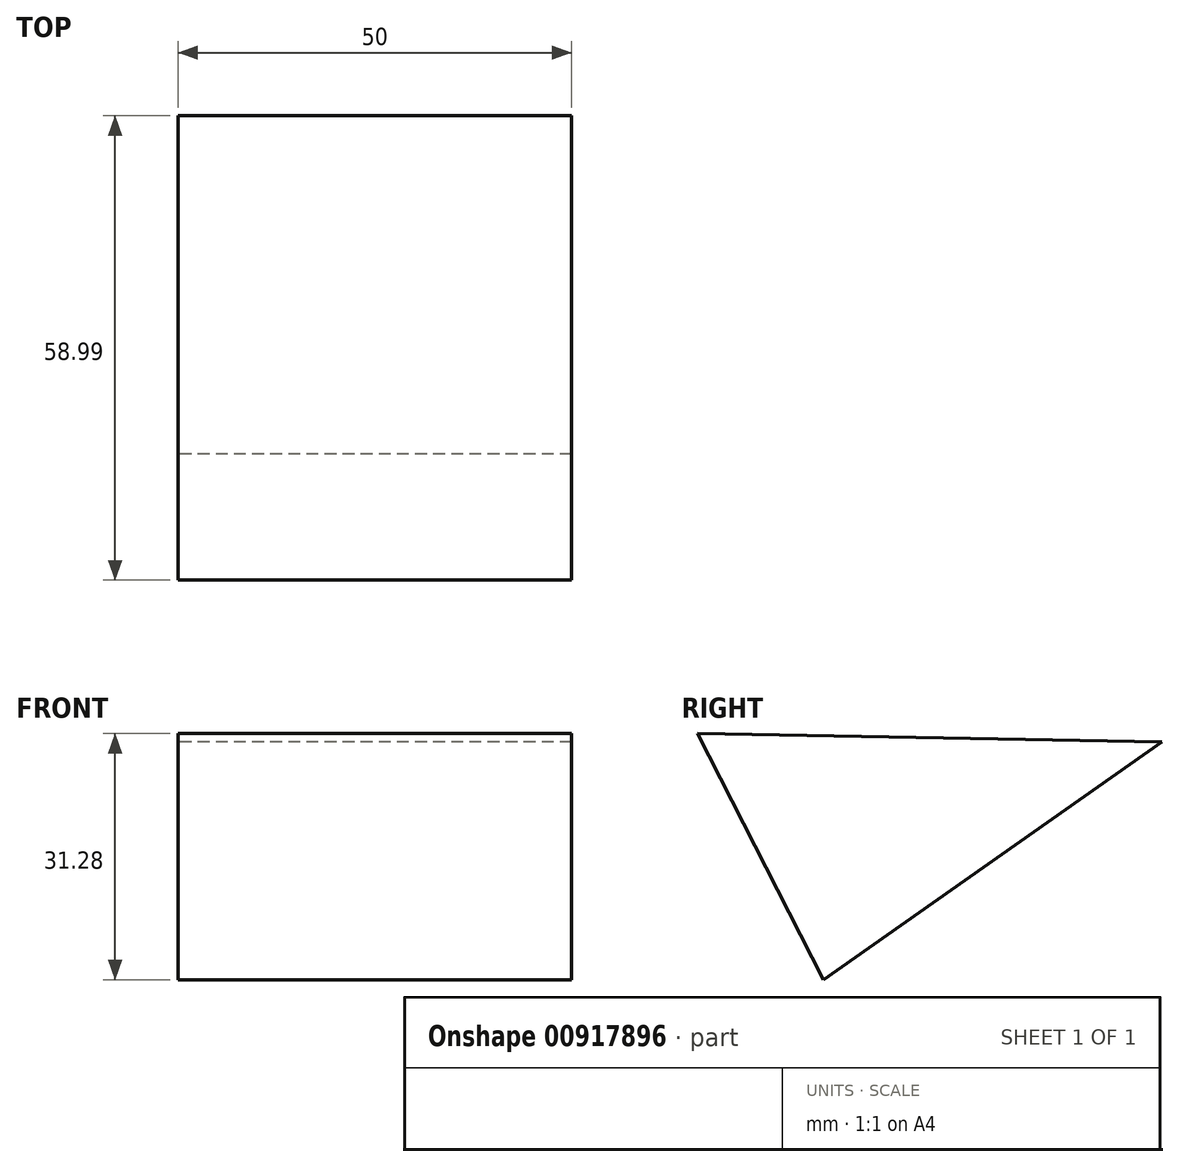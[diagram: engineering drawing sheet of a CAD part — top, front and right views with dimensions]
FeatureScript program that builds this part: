
annotation { "Feature Type Name" : "Feature", "Feature Type Description" : "" }
export const myFeature = defineFeature(function(context is Context, id is Id, definition is map)
    precondition{}
    {
        {
            var Q0;
            Q0=qCreatedBy(makeId("Right.planeOp"),FACE);
            var sketch = newSketch(context, id + "F0", { "sketchPlane" : qUnion([Q0])});
            skLineSegment(sketch, "E0", {"start": v(-51.27, 34.43) * mm, "end": v(7.72, 33.4) * mm});
            skLineSegment(sketch, "E1", {"start": v(-51.27, 34.43) * mm, "end": v(-35.27, 34.15) * mm});
            skLineSegment(sketch, "E2", {"start": v(-35.27, 34.15) * mm, "end": v(-35.27, 3.15) * mm});
            skLineSegment(sketch, "E3", {"start": v(-35.27, 3.15) * mm, "end": v(-51.27, 34.43) * mm});
            skLineSegment(sketch, "E4", {"start": v(7.72, 33.4) * mm, "end": v(-35.27, 3.15) * mm});
            skSolve(sketch);
        }
        {
            var Q0;
            Q0=makeQuery(id+"F0.imprint","IMPRINT",FACE,{"disambiguationData":[TD([[makeQuery(id+"F0.imprint","IMPRINT",EDGE,{"derivedFrom":sQuery(id+"F0.wireOp",EDGE,"E1")}),-1.0]])]});
            var Q1;
            Q1=makeQuery(id+"F0.imprint","IMPRINT",FACE,{"disambiguationData":[TD([[makeQuery(id+"F0.imprint","IMPRINT",EDGE,{"derivedFrom":sQuery(id+"F0.wireOp",EDGE,"E0")}),-1.0]])]});
            extrude(context, id + "F1", {"entities" : qUnion([Q0, Q1]), "depth" : 50 * mm, "offsetDistance" : 25 * mm});
        }
    });
